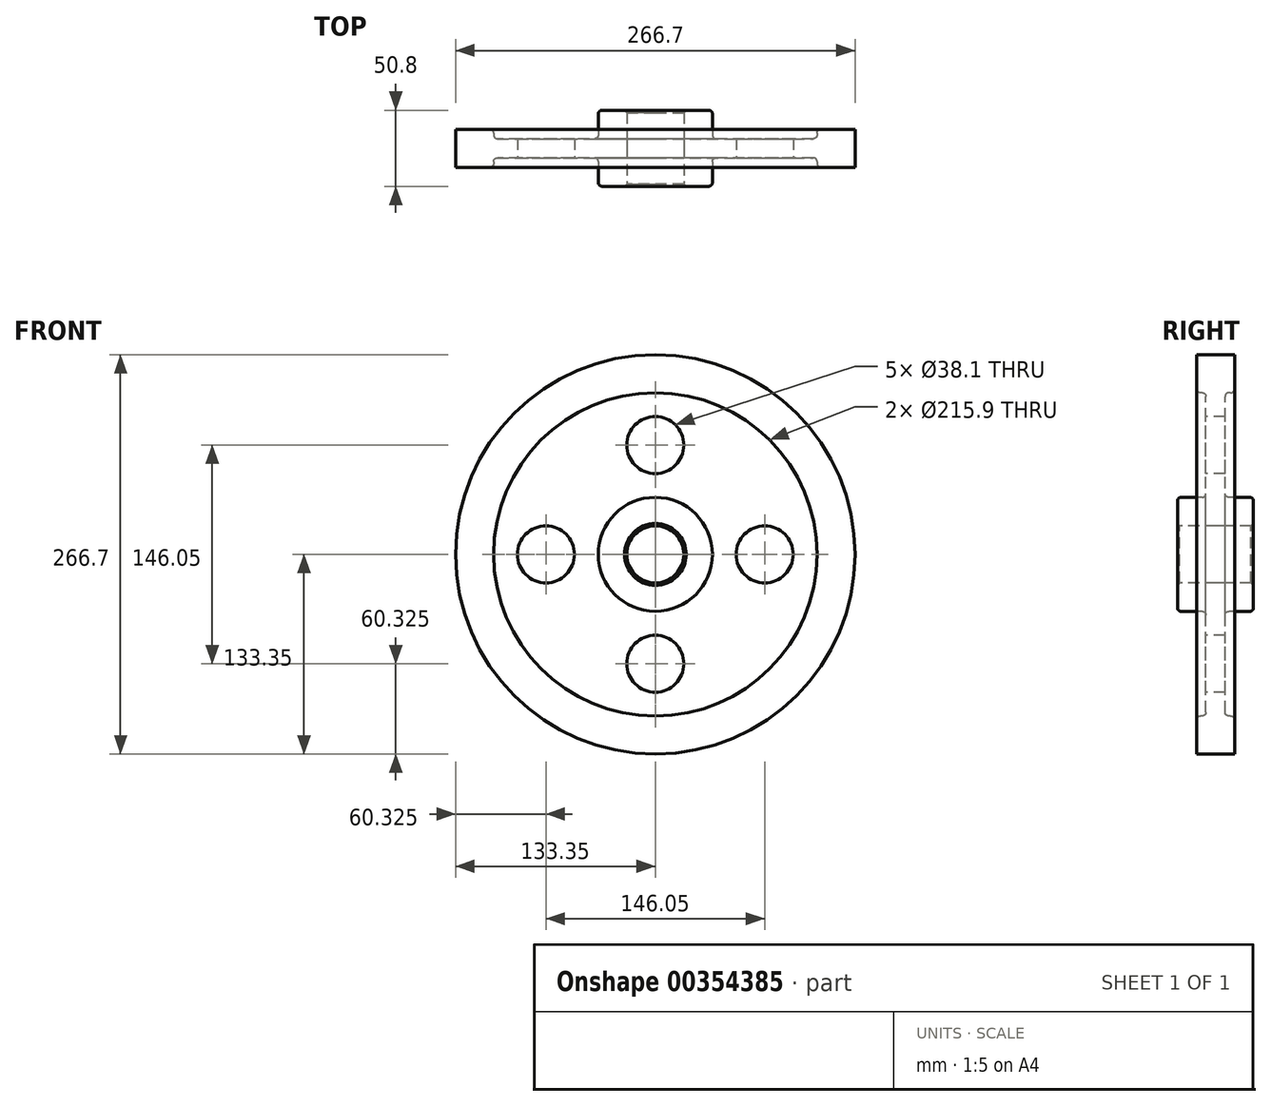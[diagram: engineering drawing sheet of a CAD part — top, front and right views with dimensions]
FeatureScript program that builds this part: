
annotation { "Feature Type Name" : "Feature", "Feature Type Description" : "" }
export const myFeature = defineFeature(function(context is Context, id is Id, definition is map)
    precondition{}
    {
        {
            var Q0;
            Q0=qCreatedBy(makeId("Right.planeOp"),FACE);
            var sketch = newSketch(context, id + "F0", { "sketchPlane" : qUnion([Q0])});
            skLineSegment(sketch, "E0", {"start": v(0, 0) * mm, "end": v(0, 28.58) * mm});
            skLineSegment(sketch, "E1", {"start": v(0, 28.58) * mm, "end": v(0, 73.03) * mm});
            skLineSegment(sketch, "E2", {"start": v(0, 73.03) * mm, "end": v(0, 120.65) * mm});
            skLineSegment(sketch, "E3.bottom", {"start": v(25.4, 19.05) * mm, "end": v(-25.4, 19.05) * mm});
            skLineSegment(sketch, "E3.top", {"start": v(25.4, 38.1) * mm, "end": v(-25.4, 38.1) * mm});
            skLineSegment(sketch, "E3.left", {"start": v(25.4, 19.05) * mm, "end": v(25.4, 38.1) * mm});
            skLineSegment(sketch, "E3.right", {"start": v(-25.4, 19.05) * mm, "end": v(-25.4, 38.1) * mm});
            skPoint(sketch, "E3.middle", {"position": v(0, 28.58) * mm});
            skLineSegment(sketch, "E4.bottom", {"start": v(12.7, 107.95) * mm, "end": v(6.35, 107.95) * mm});
            skLineSegment(sketch, "E4.top", {"start": v(12.7, 133.35) * mm, "end": v(-12.7, 133.35) * mm});
            skLineSegment(sketch, "E4.left", {"start": v(12.7, 107.95) * mm, "end": v(12.7, 133.35) * mm});
            skLineSegment(sketch, "E4.right", {"start": v(-12.7, 107.95) * mm, "end": v(-12.7, 133.35) * mm});
            skPoint(sketch, "E4.middle", {"position": v(0, 120.65) * mm});
            skLineSegment(sketch, "E5.left", {"start": v(6.35, 28.58) * mm, "end": v(6.35, 117.48) * mm});
            skLineSegment(sketch, "E5.right", {"start": v(-6.35, 28.58) * mm, "end": v(-6.35, 117.48) * mm});
            skPoint(sketch, "E5.middle", {"position": v(0, 73.03) * mm});
            skLineSegment(sketch, "E6.trimOffspring", {"start": v(-6.35, 107.95) * mm, "end": v(-12.7, 107.95) * mm});
            skLineSegment(sketch, "E7", {"start": v(0, 0) * mm, "end": v(25.91, 0) * mm});
            skSolve(sketch);
        }
        {
            var Q0;
            {var subQ4=sQuery(id+"F0.wireOp",EDGE,"E4.bottom");Q0=makeQuery(id+"F0.imprint","IMPRINT",FACE,{"disambiguationData":[TD([[makeQuery(id+"F0.imprint","IMPRINT",EDGE,{"derivedFrom":subQ4}),-1.0]])]});}
            var Q1;
            {var subQ0=sQuery(id+"F0.wireOp",EDGE,"E3.left");Q1=makeQuery(id+"F0.imprint","IMPRINT",FACE,{"disambiguationData":[TD([[makeQuery(id+"F0.imprint","IMPRINT",EDGE,{"derivedFrom":subQ0}),1.0]])]});}
            var Q2;
            {var subQ0=sQuery(id+"F0.wireOp",EDGE,"E3.right");Q2=makeQuery(id+"F0.imprint","IMPRINT",FACE,{"disambiguationData":[TD([[makeQuery(id+"F0.imprint","IMPRINT",EDGE,{"derivedFrom":subQ0}),-1.0]])]});}
            var Q3;
            Q3=sQuery(id+"F0.wireOp",EDGE,"E7");
            revolve(context, id + "F1", {"entities" : qUnion([Q0, Q1, Q2]), "axis" : qUnion([Q3]), "revolveType" : RevolveType.FULL});
        }
        {
            var Q0;
            Q0=makeQuery(id+"F1.opRevolve","SWEPT_FACE",FACE,{"disambiguationData":[OSD([sQuery(id+"F0.wireOp",EDGE,"E5.right")])]});
            var sketch = newSketch(context, id + "F2", { "sketchPlane" : qUnion([Q0])});
            skLineSegment(sketch, "E8", {"start": v(0, 0) * mm, "end": v(0, 73.03) * mm});
            skCircle(sketch, "E9", {"center": v(0, 73.03) * mm, "radius": 19.05 * mm});
            skCircle(sketch, "E10.1.0", {"center": v(-73.03, 0) * mm, "radius": 19.05 * mm});
            skCircle(sketch, "E10.2.0", {"center": v(0, -73.03) * mm, "radius": 19.05 * mm});
            skCircle(sketch, "E10.3.0", {"center": v(73.03, 0) * mm, "radius": 19.05 * mm});
            skPoint(sketch, "E10.center", {"position": v(0, 0) * mm});
            skSolve(sketch);
        }
        {
            var Q0;
            Q0=makeQuery(id+"F2.imprint","IMPRINT",FACE,{"disambiguationData":[TD([[makeQuery(id+"F2.imprint","IMPRINT",EDGE,{"derivedFrom":sQuery(id+"F2.wireOp",EDGE,"E9")}),1.0]])]});
            var Q1;
            Q1=makeQuery(id+"F2.imprint","IMPRINT",FACE,{"disambiguationData":[TD([[makeQuery(id+"F2.imprint","IMPRINT",EDGE,{"derivedFrom":sQuery(id+"F2.wireOp",EDGE,"E10.3.0")}),1.0]])]});
            var Q2;
            Q2=makeQuery(id+"F2.imprint","IMPRINT",FACE,{"disambiguationData":[TD([[makeQuery(id+"F2.imprint","IMPRINT",EDGE,{"derivedFrom":sQuery(id+"F2.wireOp",EDGE,"E10.2.0")}),1.0]])]});
            var Q3;
            Q3=makeQuery(id+"F2.imprint","IMPRINT",FACE,{"disambiguationData":[TD([[makeQuery(id+"F2.imprint","IMPRINT",EDGE,{"derivedFrom":sQuery(id+"F2.wireOp",EDGE,"E10.1.0")}),1.0]])]});
            extrude(context, id + "F3", {"entities" : qUnion([Q0, Q1, Q2, Q3]), "operationType" : NewBodyOperationType.REMOVE, "oppositeDirection" : true, "depth" : 27.7 * mm});
        }
        {
            var Q0;
            Q0=makeQuery(id+"F1.opRevolve","SWEPT_EDGE",EDGE,{"disambiguationData":[OSD([sQuery(id+"F0.wireOp",EDGE,"E5.right"),sQuery(id+"F0.wireOp",EDGE,"E6.trimOffspring")])]});
            var Q1;
            Q1=makeQuery(id+"F1.opRevolve","SWEPT_EDGE",EDGE,{"disambiguationData":[OSD([sQuery(id+"F0.wireOp",EDGE,"E3.top"),sQuery(id+"F0.wireOp",EDGE,"E5.right")])]});
            var Q2;
            Q2=makeQuery(id+"F1.opRevolve","SWEPT_EDGE",EDGE,{"disambiguationData":[OSD([sQuery(id+"F0.wireOp",EDGE,"E3.top"),sQuery(id+"F0.wireOp",EDGE,"E3.right")])]});
            var Q3;
            Q3=makeQuery(id+"F1.opRevolve","SWEPT_EDGE",EDGE,{"disambiguationData":[OSD([sQuery(id+"F0.wireOp",EDGE,"E4.bottom"),sQuery(id+"F0.wireOp",EDGE,"E5.left")])]});
            var Q4;
            Q4=makeQuery(id+"F1.opRevolve","SWEPT_EDGE",EDGE,{"disambiguationData":[OSD([sQuery(id+"F0.wireOp",EDGE,"E3.top"),sQuery(id+"F0.wireOp",EDGE,"E5.left")])]});
            var Q5;
            Q5=makeQuery(id+"F1.opRevolve","SWEPT_EDGE",EDGE,{"disambiguationData":[OSD([sQuery(id+"F0.wireOp",EDGE,"E3.top"),sQuery(id+"F0.wireOp",EDGE,"E3.left")])]});
            var Q6;
            Q6=makeQuery(id+"F1.opRevolve","SWEPT_EDGE",EDGE,{"disambiguationData":[OSD([sQuery(id+"F0.wireOp",EDGE,"E4.right"),sQuery(id+"F0.wireOp",EDGE,"E6.trimOffspring")])]});
            var Q7;
            Q7=makeQuery(id+"F1.opRevolve","SWEPT_EDGE",EDGE,{"disambiguationData":[OSD([sQuery(id+"F0.wireOp",EDGE,"E4.bottom"),sQuery(id+"F0.wireOp",EDGE,"E4.left")])]});
            fillet(context, id + "F4", {"entities" : qUnion([Q0, Q1, Q2, Q3, Q4, Q5, Q6, Q7]), "radius" : 2.54 * mm, "tangentPropagation" : true, "allowEdgeOverflow" : false});
        }
        {
            var Q0;
            Q0=makeQuery(id+"F1.opRevolve","SWEPT_EDGE",EDGE,{"disambiguationData":[OSD([sQuery(id+"F0.wireOp",EDGE,"E3.bottom"),sQuery(id+"F0.wireOp",EDGE,"E3.right")])]});
            var Q1;
            Q1=makeQuery(id+"F1.opRevolve","SWEPT_EDGE",EDGE,{"disambiguationData":[OSD([sQuery(id+"F0.wireOp",EDGE,"E3.bottom"),sQuery(id+"F0.wireOp",EDGE,"E3.left")])]});
            chamfer(context, id + "F5", {"entities" : qUnion([Q0, Q1]), "width" : 1.59 * mm, "tangentPropagation" : true});
        }
    });
